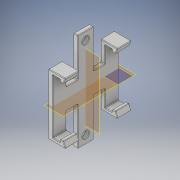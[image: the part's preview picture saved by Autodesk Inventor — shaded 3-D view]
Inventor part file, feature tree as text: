
AUTODESK INVENTOR PART (.ipt)
format: ipt  version: 2019 (Build 230136000, 136)  size: 398,336 bytes
history: native  units: in
note: dims shown in document units (in); Inventor stores cm internally (conversion verified against a paired STEP export)
features: extrude x7, sketch x7, plane x3, mirror x3, fillet x1, projected_geometry x1
ambient origin geometry x8: Origin, YZ Plane, XZ Plane, XY Plane, X Axis, Y Axis, Z Axis, Center Point
bodies: Solid1 (feature_tree)
feature tree (22):
  extrude  "Extrusion1"  Depth=0.5118in
  extrude  "Extrusion2"  Depth=0.5118in
  extrude  "Extrusion3"  Depth=0.2717in TaperAngle=0.0deg
  extrude  "Extrusion4"  Depth=0.0866in
  plane  "Work Plane2"
  mirror  "Mirror1"
  extrude  "Extrusion5"  Depth=0.1181in
  plane  "Work Plane3"
  mirror  "Mirror2"
  extrude  "Extrusion6"  Depth=0.7874in
  extrude  "Extrusion7"  Depth=0.1575in
  plane  "Work Plane4"
  mirror  "Mirror3"
  fillet  "Fillet1"  Radius=0.5906in
  sketch  "Sketch1"  dims[d0=2.0157in d1=0.5118in]
  sketch  "Sketch3"  dims[d2=0.1575in d3=0.0in d4=0.5118in]
  sketch  "Sketch4"  dims[d5=0.1181in d6=0.2717in d7=0.0in]
  projected_geometry  "Projected Loop1"
  sketch  "Sketch5"  dims[d8=0.1575in d9=0.0in d10=0.0866in]
  sketch  "Sketch6"  dims[d11=0.1181in d12=0.4535in]
  sketch  "Sketch7"  dims[d13=0.1575in d14=0.0in d15=0.7874in]
  sketch  "Sketch8"  dims[d16=1.4173in d17=0.0in d18=0.1575in d19=0.5906in d20=1.4173in d21=0.0in d22=0.248in d23=1.4173in d24=0.0in d25=0.0197in]
